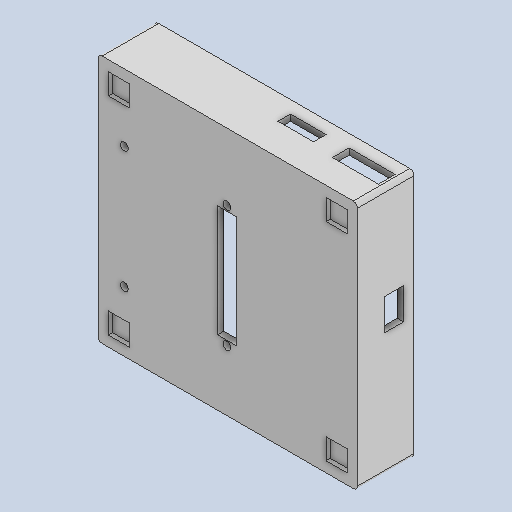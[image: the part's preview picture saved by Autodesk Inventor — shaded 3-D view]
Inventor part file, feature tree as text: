
AUTODESK INVENTOR PART (.ipt)
format: ipt  version: 2023 (Build 270158000, 158)  size: 475,136 bytes
history: native  units: mm
features: other x54, extrude x9, sketch x9, fillet x1
ambient origin geometry x8: Origin, YZ Plane, XZ Plane, XY Plane, X Axis, Y Axis, Z Axis, Center Point
bodies: Solide1 (feature_tree)
feature tree (73):
  extrude  "Extrusion1"  Depth=92.0mm
  extrude  "Extrusion2"  Depth=105.0mm
  extrude  "Extrusion4"  Depth=13.0mm
  extrude  "Extrusion5"  Depth=21.0mm
  extrude  "Extrusion6"  Depth=2.0mm
  extrude  "Extrusion7"  Depth=1.3mm
  extrude  "Extrusion8"  Depth=1.3mm
  extrude  "Extrusion10"  Depth=3.0mm
  fillet  "Congé1"  Radius=3.0mm
  extrude  "Extrusion11"  Depth=3.0mm
  sketch  "Esquisse1"
  sketch  "Esquisse2"
  sketch  "Esquisse4"
  other  "Référence1"
  other  "Référence2"
  other  "Référence3"
  other  "Référence4"
  other  "Référence5"
  other  "Référence6"
  other  "Référence7"
  other  "Référence8"
  other  "Référence9"
  other  "Référence10"
  other  "Référence11"
  other  "Référence12"
  other  "Référence13"
  other  "Référence14"
  other  "Référence15"
  other  "Référence16"
  other  "Référence17"
  other  "Référence18"
  other  "Référence19"
  other  "Référence20"
  other  "Référence21"
  other  "Référence22"
  other  "Référence23"
  other  "Référence24"
  other  "Référence25"
  other  "Référence26"
  other  "Référence27"
  other  "Référence28"
  other  "Référence29"
  other  "Référence30"
  other  "Référence31"
  other  "Référence32"
  other  "Référence33"
  sketch  "Esquisse5"
  other  "Référence34"
  other  "Référence35"
  other  "Référence36"
  other  "Référence37"
  other  "Référence38"
  other  "Référence39"
  other  "Référence40"
  other  "Référence41"
  other  "Référence42"
  other  "Référence43"
  other  "Référence44"
  other  "Référence45"
  other  "Référence46"
  other  "Référence47"
  other  "Référence48"
  other  "Référence49"
  other  "Référence50"
  other  "Référence51"
  sketch  "Esquisse6"
  sketch  "Esquisse7"
  sketch  "Esquisse8"
  sketch  "Esquisse10"
  sketch  "Esquisse11"
  other  "<userpath>\OneDrive\ISMIN 3A\3D\Ensemble1.iam"
  other  "Ensemble1.iam"
  other  "Raspberry_Pi_3_Light_Version:1"
